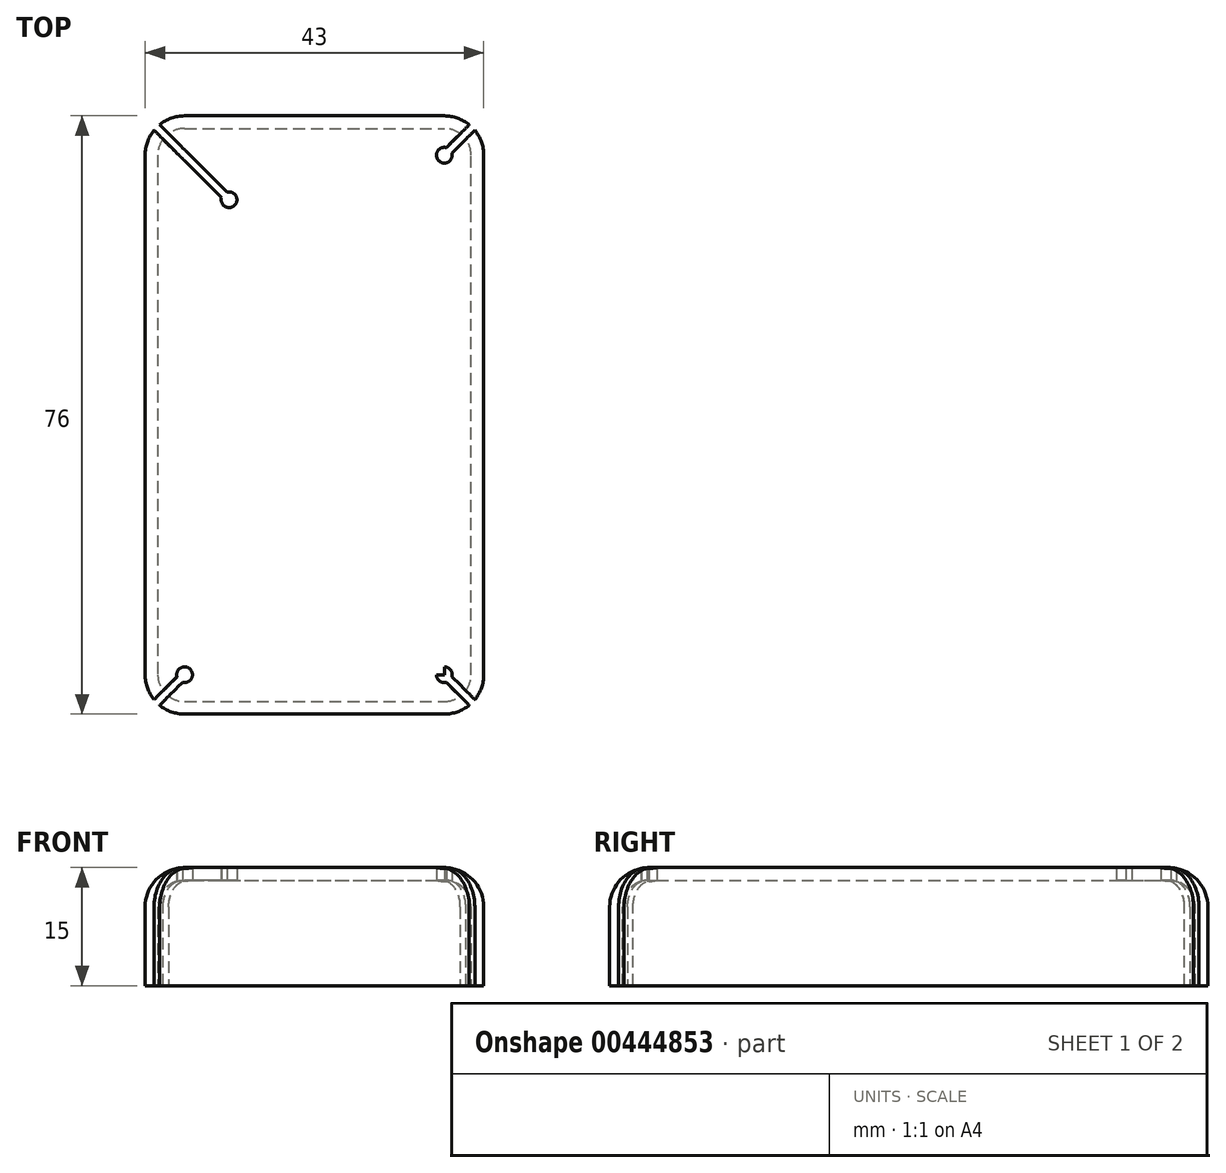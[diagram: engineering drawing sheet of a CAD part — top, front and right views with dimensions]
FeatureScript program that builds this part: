
annotation { "Feature Type Name" : "Feature", "Feature Type Description" : "" }
export const myFeature = defineFeature(function(context is Context, id is Id, definition is map)
    precondition{}
    {
        {
            var Q0;
            Q0=qCreatedBy(makeId("Top.planeOp"),FACE);
            var sketch = newSketch(context, id + "F0", { "sketchPlane" : qUnion([Q0])});
            skLineSegment(sketch, "E0.bottom", {"start": v(-21.5, 38) * mm, "end": v(21.5, 38) * mm});
            skLineSegment(sketch, "E0.top", {"start": v(-21.5, -38) * mm, "end": v(21.5, -38) * mm});
            skLineSegment(sketch, "E0.left", {"start": v(-21.5, 38) * mm, "end": v(-21.5, -38) * mm});
            skLineSegment(sketch, "E0.right", {"start": v(21.5, 38) * mm, "end": v(21.5, -38) * mm});
            skPoint(sketch, "E0.middle", {"position": v(0, 0) * mm});
            skSolve(sketch);
        }
        {
            var Q0;
            Q0 = qSketchRegion(id + "F0", true);
            extrude(context, id + "F1", {"entities" : qUnion([Q0]), "depth" : 15 * mm});
        }
        {
            var Q0;
            Q0=makeQuery(id+"F1.opExtrude","SWEPT_EDGE",EDGE,{"disambiguationData":[OSD([sQuery(id+"F0.wireOp",EDGE,"E0.top"),sQuery(id+"F0.wireOp",EDGE,"E0.left")])]});
            var Q1;
            Q1=makeQuery(id+"F1.opExtrude","SWEPT_EDGE",EDGE,{"disambiguationData":[OSD([sQuery(id+"F0.wireOp",EDGE,"E0.top"),sQuery(id+"F0.wireOp",EDGE,"E0.right")])]});
            var Q2;
            Q2=makeQuery(id+"F1.opExtrude","SWEPT_EDGE",EDGE,{"disambiguationData":[OSD([sQuery(id+"F0.wireOp",EDGE,"E0.bottom"),sQuery(id+"F0.wireOp",EDGE,"E0.right")])]});
            var Q3;
            Q3=makeQuery(id+"F1.opExtrude","SWEPT_EDGE",EDGE,{"disambiguationData":[OSD([sQuery(id+"F0.wireOp",EDGE,"E0.bottom"),sQuery(id+"F0.wireOp",EDGE,"E0.left")])]});
            var Q4;
            Q4=makeQuery(id+"F1.opExtrude","CAP_FACE",FACE,{"disambiguationData":[OSD([sQuery(id+"F0.wireOp",EDGE,"E0.bottom"),sQuery(id+"F0.wireOp",EDGE,"E0.top"),sQuery(id+"F0.wireOp",EDGE,"E0.left"),sQuery(id+"F0.wireOp",EDGE,"E0.right")])],"isStart":false});
            fillet(context, id + "F2", {"entities" : qUnion([Q0, Q1, Q2, Q3, Q4]), "radius" : 5 * mm, "tangentPropagation" : true, "allowEdgeOverflow" : false});
        }
        {
            var Q0;
            Q0=makeQuery(id+"F1.opExtrude","CAP_FACE",FACE,{"disambiguationData":[OSD([sQuery(id+"F0.wireOp",EDGE,"E0.bottom"),sQuery(id+"F0.wireOp",EDGE,"E0.top"),sQuery(id+"F0.wireOp",EDGE,"E0.left"),sQuery(id+"F0.wireOp",EDGE,"E0.right")])],"isStart":true});
            shell(context, id + "F3", {"entities" : qUnion([Q0]), "thickness" : 1.6 * mm});
        }
        {
            var Q0;
            Q0=qCreatedBy(makeId("Top.planeOp"),FACE);
            var sketch = newSketch(context, id + "F4", { "sketchPlane" : qUnion([Q0])});
            skLineSegment(sketch, "E1.0.0", {"start": v(-16.5, -33) * mm, "end": v(16.5, -33) * mm});
            skLineSegment(sketch, "E1.0.1", {"start": v(16.5, -33) * mm, "end": v(16.5, 33) * mm});
            skLineSegment(sketch, "E1.0.2", {"start": v(16.5, 33) * mm, "end": v(-16.5, 33) * mm});
            skLineSegment(sketch, "E1.0.3", {"start": v(-16.5, 33) * mm, "end": v(-16.5, -33) * mm});
            skCircle(sketch, "E2", {"center": v(-16.5, -33) * mm, "radius": 1 * mm});
            skCircle(sketch, "E3", {"center": v(16.5, 33) * mm, "radius": 1 * mm});
            skCircle(sketch, "E4", {"center": v(16.5, -33) * mm, "radius": 1 * mm});
            skLineSegment(sketch, "E5", {"start": v(-16.5, 33) * mm, "end": v(-10.84, 27.34) * mm});
            skCircle(sketch, "E6", {"center": v(-10.84, 27.34) * mm, "radius": 1 * mm});
            skPoint(sketch, "E7.0", {"position": v(20.04, 36.54) * mm});
            skLineSegment(sketch, "E8", {"start": v(16.5, 33) * mm, "end": v(20.04, 36.54) * mm});
            skLineSegment(sketch, "E9", {"start": v(20.04, 36.54) * mm, "end": v(19.68, 36.89) * mm});
            skLineSegment(sketch, "E10", {"start": v(19.68, 36.89) * mm, "end": v(15.63, 32.84) * mm});
            skLineSegment(sketch, "E11", {"start": v(20.04, 36.54) * mm, "end": v(20.39, 36.18) * mm});
            skLineSegment(sketch, "E12", {"start": v(20.39, 36.18) * mm, "end": v(16.51, 32.3) * mm});
            skLineSegment(sketch, "E13", {"start": v(16.5, 33) * mm, "end": v(16.85, 32.65) * mm});
            skLineSegment(sketch, "E14", {"start": v(16.5, 33) * mm, "end": v(16.15, 33.35) * mm});
            skPoint(sketch, "E15.0", {"position": v(-20.04, 36.54) * mm});
            skLineSegment(sketch, "E16", {"start": v(-16.5, 33) * mm, "end": v(-20.04, 36.54) * mm});
            skLineSegment(sketch, "E17", {"start": v(-20.04, 36.54) * mm, "end": v(-19.68, 36.89) * mm});
            skLineSegment(sketch, "E18", {"start": v(-19.68, 36.89) * mm, "end": v(-11, 28.2) * mm});
            skLineSegment(sketch, "E19", {"start": v(-20.04, 36.54) * mm, "end": v(-20.39, 36.18) * mm});
            skLineSegment(sketch, "E20", {"start": v(-20.39, 36.18) * mm, "end": v(-11.5, 27.3) * mm});
            skLineSegment(sketch, "E21", {"start": v(-10.84, 27.34) * mm, "end": v(-11.2, 26.99) * mm});
            skLineSegment(sketch, "E22", {"start": v(-10.84, 27.34) * mm, "end": v(-10.49, 27.7) * mm});
            skLineSegment(sketch, "E23.MirrorCS", {"start": v(16.5, -33) * mm, "end": v(16.85, -32.65) * mm});
            skLineSegment(sketch, "E24.MirrorCS", {"start": v(16.5, -33) * mm, "end": v(16.15, -33.35) * mm});
            skLineSegment(sketch, "E25.MirrorCS", {"start": v(20.04, -36.54) * mm, "end": v(20.39, -36.18) * mm});
            skLineSegment(sketch, "E26.MirrorCS", {"start": v(20.04, -36.54) * mm, "end": v(19.68, -36.89) * mm});
            skLineSegment(sketch, "E27.MirrorCS", {"start": v(19.68, -36.89) * mm, "end": v(15.63, -32.84) * mm});
            skPoint(sketch, "E28.MirrorP", {"position": v(20.04, -36.54) * mm});
            skLineSegment(sketch, "E29.MirrorCS", {"start": v(20.39, -36.18) * mm, "end": v(16.51, -32.3) * mm});
            skLineSegment(sketch, "E30.MirrorCS", {"start": v(16.5, -33) * mm, "end": v(20.04, -36.54) * mm});
            skLineSegment(sketch, "E31.MirrorCS", {"start": v(-16.5, -33) * mm, "end": v(-16.85, -32.65) * mm});
            skLineSegment(sketch, "E32.MirrorCS", {"start": v(-16.5, -33) * mm, "end": v(-16.15, -33.35) * mm});
            skLineSegment(sketch, "E33.MirrorCS", {"start": v(-20.04, -36.54) * mm, "end": v(-20.39, -36.18) * mm});
            skLineSegment(sketch, "E34.MirrorCS", {"start": v(-20.04, -36.54) * mm, "end": v(-19.68, -36.89) * mm});
            skLineSegment(sketch, "E35.MirrorCS", {"start": v(-16.5, -33) * mm, "end": v(-16.5, 33) * mm});
            skLineSegment(sketch, "E36.MirrorCS", {"start": v(-20.39, -36.18) * mm, "end": v(-16.51, -32.3) * mm});
            skPoint(sketch, "E37.MirrorP", {"position": v(-20.04, -36.54) * mm});
            skLineSegment(sketch, "E38.MirrorCS", {"start": v(-19.68, -36.89) * mm, "end": v(-15.63, -32.84) * mm});
            skLineSegment(sketch, "E39.MirrorCS", {"start": v(16.5, -33) * mm, "end": v(-16.5, -33) * mm});
            skLineSegment(sketch, "E40.MirrorCS", {"start": v(-16.5, -33) * mm, "end": v(-20.04, -36.54) * mm});
            skSolve(sketch);
        }
        {
            var Q0;
            {var subQ5=sQuery(id+"F4.wireOp",EDGE,"E9");Q0=makeQuery(id+"F4.imprint","IMPRINT",FACE,{"disambiguationData":[TD([[makeQuery(id+"F4.imprint","IMPRINT",EDGE,{"derivedFrom":subQ5}),1.0]])]});}
            var Q1;
            {var subQ5=sQuery(id+"F4.wireOp",EDGE,"E11");Q1=makeQuery(id+"F4.imprint","IMPRINT",FACE,{"disambiguationData":[TD([[makeQuery(id+"F4.imprint","IMPRINT",EDGE,{"derivedFrom":subQ5}),-1.0]])]});}
            var Q2;
            {var subQ0=sQuery(id+"F4.wireOp",EDGE,"E10");var subQ1=sQuery(id+"F4.wireOp",EDGE,"E1.0.2");var subQ2=makeQuery(id+"F4.imprint","INTERSECT",VERTEX,{"derivedFrom":[subQ1,subQ0]});Q2=makeQuery(id+"F4.imprint","IMPRINT",FACE,{"disambiguationData":[TD([[makeQuery(id+"F4.imprint","IMPRINT",EDGE,{"disambiguationData":[TD([[subQ2,-1.0]])],"derivedFrom":subQ1}),-1.0]])]});}
            var Q3;
            {var subQ5=sQuery(id+"F4.wireOp",EDGE,"E14");Q3=makeQuery(id+"F4.imprint","IMPRINT",FACE,{"disambiguationData":[TD([[makeQuery(id+"F4.imprint","IMPRINT",EDGE,{"derivedFrom":subQ5}),-1.0]])]});}
            var Q4;
            {var subQ5=sQuery(id+"F4.wireOp",EDGE,"E13");Q4=makeQuery(id+"F4.imprint","IMPRINT",FACE,{"disambiguationData":[TD([[makeQuery(id+"F4.imprint","IMPRINT",EDGE,{"derivedFrom":subQ5}),1.0]])]});}
            var Q5;
            {var subQ0=sQuery(id+"F4.wireOp",EDGE,"E13");Q5=makeQuery(id+"F4.imprint","IMPRINT",FACE,{"disambiguationData":[TD([[makeQuery(id+"F4.imprint","IMPRINT",EDGE,{"derivedFrom":subQ0}),-1.0]])]});}
            var Q6;
            {var subQ0=sQuery(id+"F4.wireOp",EDGE,"E1.0.2");var subQ5=makeQuery(id+"F4.imprint","INTERSECT",VERTEX,{"derivedFrom":[subQ0,sQuery(id+"F4.wireOp",EDGE,"E10")]});Q6=makeQuery(id+"F4.imprint","IMPRINT",FACE,{"disambiguationData":[TD([[makeQuery(id+"F4.imprint","IMPRINT",EDGE,{"disambiguationData":[TD([[subQ5,-1.0]])],"derivedFrom":subQ0}),1.0]])]});}
            var Q7;
            {var subQ0=sQuery(id+"F4.wireOp",EDGE,"E14");Q7=makeQuery(id+"F4.imprint","IMPRINT",FACE,{"disambiguationData":[TD([[makeQuery(id+"F4.imprint","IMPRINT",EDGE,{"derivedFrom":subQ0}),1.0]])]});}
            var Q8;
            {var subQ0=sQuery(id+"F4.wireOp",EDGE,"E16");Q8=makeQuery(id+"F4.imprint","IMPRINT",FACE,{"disambiguationData":[TD([[makeQuery(id+"F4.imprint","IMPRINT",EDGE,{"derivedFrom":subQ0}),1.0]])]});}
            var Q9;
            {var subQ0=sQuery(id+"F4.wireOp",EDGE,"E16");Q9=makeQuery(id+"F4.imprint","IMPRINT",FACE,{"disambiguationData":[TD([[makeQuery(id+"F4.imprint","IMPRINT",EDGE,{"derivedFrom":subQ0}),-1.0]])]});}
            var Q10;
            {var subQ0=sQuery(id+"F4.wireOp",EDGE,"E5");var subQ5=sQuery(id+"F4.wireOp",EDGE,"E6");var subQ6=makeQuery(id+"F4.imprint","INTERSECT",VERTEX,{"derivedFrom":[subQ0,subQ5]});Q10=makeQuery(id+"F4.imprint","IMPRINT",FACE,{"disambiguationData":[TD([[makeQuery(id+"F4.imprint","IMPRINT",EDGE,{"disambiguationData":[TD([[subQ6,1.0]])],"derivedFrom":subQ5}),-1.0]])]});}
            var Q11;
            {var subQ0=sQuery(id+"F4.wireOp",EDGE,"E5");var subQ5=sQuery(id+"F4.wireOp",EDGE,"E6");var subQ6=makeQuery(id+"F4.imprint","INTERSECT",VERTEX,{"derivedFrom":[subQ0,subQ5]});Q11=makeQuery(id+"F4.imprint","IMPRINT",FACE,{"disambiguationData":[TD([[makeQuery(id+"F4.imprint","IMPRINT",EDGE,{"disambiguationData":[TD([[subQ6,-1.0]])],"derivedFrom":subQ5}),-1.0]])]});}
            var Q12;
            {var subQ0=sQuery(id+"F4.wireOp",EDGE,"E22");Q12=makeQuery(id+"F4.imprint","IMPRINT",FACE,{"disambiguationData":[TD([[makeQuery(id+"F4.imprint","IMPRINT",EDGE,{"derivedFrom":subQ0}),1.0]])]});}
            var Q13;
            {var subQ0=sQuery(id+"F4.wireOp",EDGE,"E18");var subQ1=sQuery(id+"F4.wireOp",EDGE,"E6");var subQ2=makeQuery(id+"F4.imprint","INTERSECT",VERTEX,{"disambiguationData":[OD(0.0)],"derivedFrom":[subQ1,subQ0]});Q13=makeQuery(id+"F4.imprint","IMPRINT",FACE,{"disambiguationData":[TD([[makeQuery(id+"F4.imprint","IMPRINT",EDGE,{"disambiguationData":[TD([[subQ2,-1.0]])],"derivedFrom":subQ1}),1.0]])]});}
            var Q14;
            {var subQ0=sQuery(id+"F4.wireOp",EDGE,"E21");Q14=makeQuery(id+"F4.imprint","IMPRINT",FACE,{"disambiguationData":[TD([[makeQuery(id+"F4.imprint","IMPRINT",EDGE,{"derivedFrom":subQ0}),1.0]])]});}
            var Q15;
            {var subQ0=sQuery(id+"F4.wireOp",EDGE,"E21");Q15=makeQuery(id+"F4.imprint","IMPRINT",FACE,{"disambiguationData":[TD([[makeQuery(id+"F4.imprint","IMPRINT",EDGE,{"derivedFrom":subQ0}),-1.0]])]});}
            var Q16;
            {var subQ0=sQuery(id+"F4.wireOp",EDGE,"E20");var subQ1=sQuery(id+"F4.wireOp",EDGE,"E6");var subQ2=makeQuery(id+"F4.imprint","INTERSECT",VERTEX,{"disambiguationData":[OD(0.0)],"derivedFrom":[subQ1,subQ0]});Q16=makeQuery(id+"F4.imprint","IMPRINT",FACE,{"disambiguationData":[TD([[makeQuery(id+"F4.imprint","IMPRINT",EDGE,{"disambiguationData":[TD([[subQ2,1.0]])],"derivedFrom":subQ1}),1.0]])]});}
            var Q17;
            {var subQ0=sQuery(id+"F4.wireOp",EDGE,"E25.MirrorCS");Q17=makeQuery(id+"F4.imprint","IMPRINT",FACE,{"disambiguationData":[TD([[makeQuery(id+"F4.imprint","IMPRINT",EDGE,{"derivedFrom":subQ0}),1.0]])]});}
            var Q18;
            {var subQ0=sQuery(id+"F4.wireOp",EDGE,"E26.MirrorCS");Q18=makeQuery(id+"F4.imprint","IMPRINT",FACE,{"disambiguationData":[TD([[makeQuery(id+"F4.imprint","IMPRINT",EDGE,{"derivedFrom":subQ0}),-1.0]])]});}
            var Q19;
            {var subQ0=sQuery(id+"F4.wireOp",EDGE,"E24.MirrorCS");Q19=makeQuery(id+"F4.imprint","IMPRINT",FACE,{"disambiguationData":[TD([[makeQuery(id+"F4.imprint","IMPRINT",EDGE,{"derivedFrom":subQ0}),1.0]])]});}
            var Q20;
            {var subQ0=sQuery(id+"F4.wireOp",EDGE,"E23.MirrorCS");Q20=makeQuery(id+"F4.imprint","IMPRINT",FACE,{"disambiguationData":[TD([[makeQuery(id+"F4.imprint","IMPRINT",EDGE,{"derivedFrom":subQ0}),-1.0]])]});}
            var Q21;
            {var subQ0=sQuery(id+"F4.wireOp",EDGE,"E23.MirrorCS");Q21=makeQuery(id+"F4.imprint","IMPRINT",FACE,{"disambiguationData":[TD([[makeQuery(id+"F4.imprint","IMPRINT",EDGE,{"derivedFrom":subQ0}),1.0]])]});}
            var Q22;
            {var subQ1=sQuery(id+"F4.wireOp",EDGE,"E1.0.1");var subQ3=sQuery(id+"F4.wireOp",EDGE,"E4");var subQ4=makeQuery(id+"F4.imprint","INTERSECT",VERTEX,{"derivedFrom":[subQ1,subQ3]});Q22=makeQuery(id+"F4.imprint","IMPRINT",FACE,{"disambiguationData":[TD([[makeQuery(id+"F4.imprint","IMPRINT",EDGE,{"disambiguationData":[TD([[subQ4,1.0]])],"derivedFrom":subQ3}),-1.0]])]});}
            var Q23;
            {var subQ0=sQuery(id+"F4.wireOp",EDGE,"E27.MirrorCS");var subQ1=makeQuery(id+"F4.imprint","INTERSECT",VERTEX,{"derivedFrom":[sQuery(id+"F4.wireOp",EDGE,"E24.MirrorCS"),subQ0]});Q23=makeQuery(id+"F4.imprint","IMPRINT",FACE,{"disambiguationData":[TD([[makeQuery(id+"F4.imprint","IMPRINT",EDGE,{"disambiguationData":[TD([[subQ1,1.0]])],"derivedFrom":subQ0}),1.0]])]});}
            var Q24;
            {var subQ0=sQuery(id+"F4.wireOp",EDGE,"E24.MirrorCS");Q24=makeQuery(id+"F4.imprint","IMPRINT",FACE,{"disambiguationData":[TD([[makeQuery(id+"F4.imprint","IMPRINT",EDGE,{"derivedFrom":subQ0}),-1.0]])]});}
            var Q25;
            {var subQ0=sQuery(id+"F4.wireOp",EDGE,"E39.MirrorCS");var subQ1=sQuery(id+"F4.wireOp",EDGE,"E2");var subQ2=makeQuery(id+"F4.imprint","INTERSECT",VERTEX,{"derivedFrom":[subQ1,subQ0]});Q25=makeQuery(id+"F4.imprint","IMPRINT",FACE,{"disambiguationData":[TD([[makeQuery(id+"F4.imprint","IMPRINT",EDGE,{"disambiguationData":[TD([[subQ2,-1.0]])],"derivedFrom":subQ1}),1.0]])]});}
            var Q26;
            {var subQ0=sQuery(id+"F4.wireOp",EDGE,"E32.MirrorCS");Q26=makeQuery(id+"F4.imprint","IMPRINT",FACE,{"disambiguationData":[TD([[makeQuery(id+"F4.imprint","IMPRINT",EDGE,{"derivedFrom":subQ0}),1.0]])]});}
            var Q27;
            {var subQ0=sQuery(id+"F4.wireOp",EDGE,"E38.MirrorCS");var subQ1=sQuery(id+"F4.wireOp",EDGE,"E2");var subQ2=makeQuery(id+"F4.imprint","INTERSECT",VERTEX,{"derivedFrom":[subQ1,subQ0]});Q27=makeQuery(id+"F4.imprint","IMPRINT",FACE,{"disambiguationData":[TD([[makeQuery(id+"F4.imprint","IMPRINT",EDGE,{"disambiguationData":[TD([[subQ2,-1.0]])],"derivedFrom":subQ1}),1.0]])]});}
            var Q28;
            {var subQ5=sQuery(id+"F4.wireOp",EDGE,"E34.MirrorCS");Q28=makeQuery(id+"F4.imprint","IMPRINT",FACE,{"disambiguationData":[TD([[makeQuery(id+"F4.imprint","IMPRINT",EDGE,{"derivedFrom":subQ5}),1.0]])]});}
            var Q29;
            {var subQ5=sQuery(id+"F4.wireOp",EDGE,"E33.MirrorCS");Q29=makeQuery(id+"F4.imprint","IMPRINT",FACE,{"disambiguationData":[TD([[makeQuery(id+"F4.imprint","IMPRINT",EDGE,{"derivedFrom":subQ5}),-1.0]])]});}
            var Q30;
            {var subQ0=sQuery(id+"F4.wireOp",EDGE,"E31.MirrorCS");Q30=makeQuery(id+"F4.imprint","IMPRINT",FACE,{"disambiguationData":[TD([[makeQuery(id+"F4.imprint","IMPRINT",EDGE,{"derivedFrom":subQ0}),-1.0]])]});}
            var Q31;
            {var subQ0=sQuery(id+"F4.wireOp",EDGE,"E31.MirrorCS");Q31=makeQuery(id+"F4.imprint","IMPRINT",FACE,{"disambiguationData":[TD([[makeQuery(id+"F4.imprint","IMPRINT",EDGE,{"derivedFrom":subQ0}),1.0]])]});}
            var Q32;
            {var subQ5=sQuery(id+"F4.wireOp",EDGE,"E32.MirrorCS");Q32=makeQuery(id+"F4.imprint","IMPRINT",FACE,{"disambiguationData":[TD([[makeQuery(id+"F4.imprint","IMPRINT",EDGE,{"derivedFrom":subQ5}),-1.0]])]});}
            extrude(context, id + "F5", {"entities" : qUnion([Q0, Q1, Q2, Q3, Q4, Q5, Q6, Q7, Q8, Q9, Q10, Q11, Q12, Q13, Q14, Q15, Q16, Q17, Q18, Q19, Q20, Q21, Q22, Q23, Q24, Q25, Q26, Q27, Q28, Q29, Q30, Q31, Q32]), "operationType" : NewBodyOperationType.REMOVE, "depth" : 25 * mm});
        }
    });
